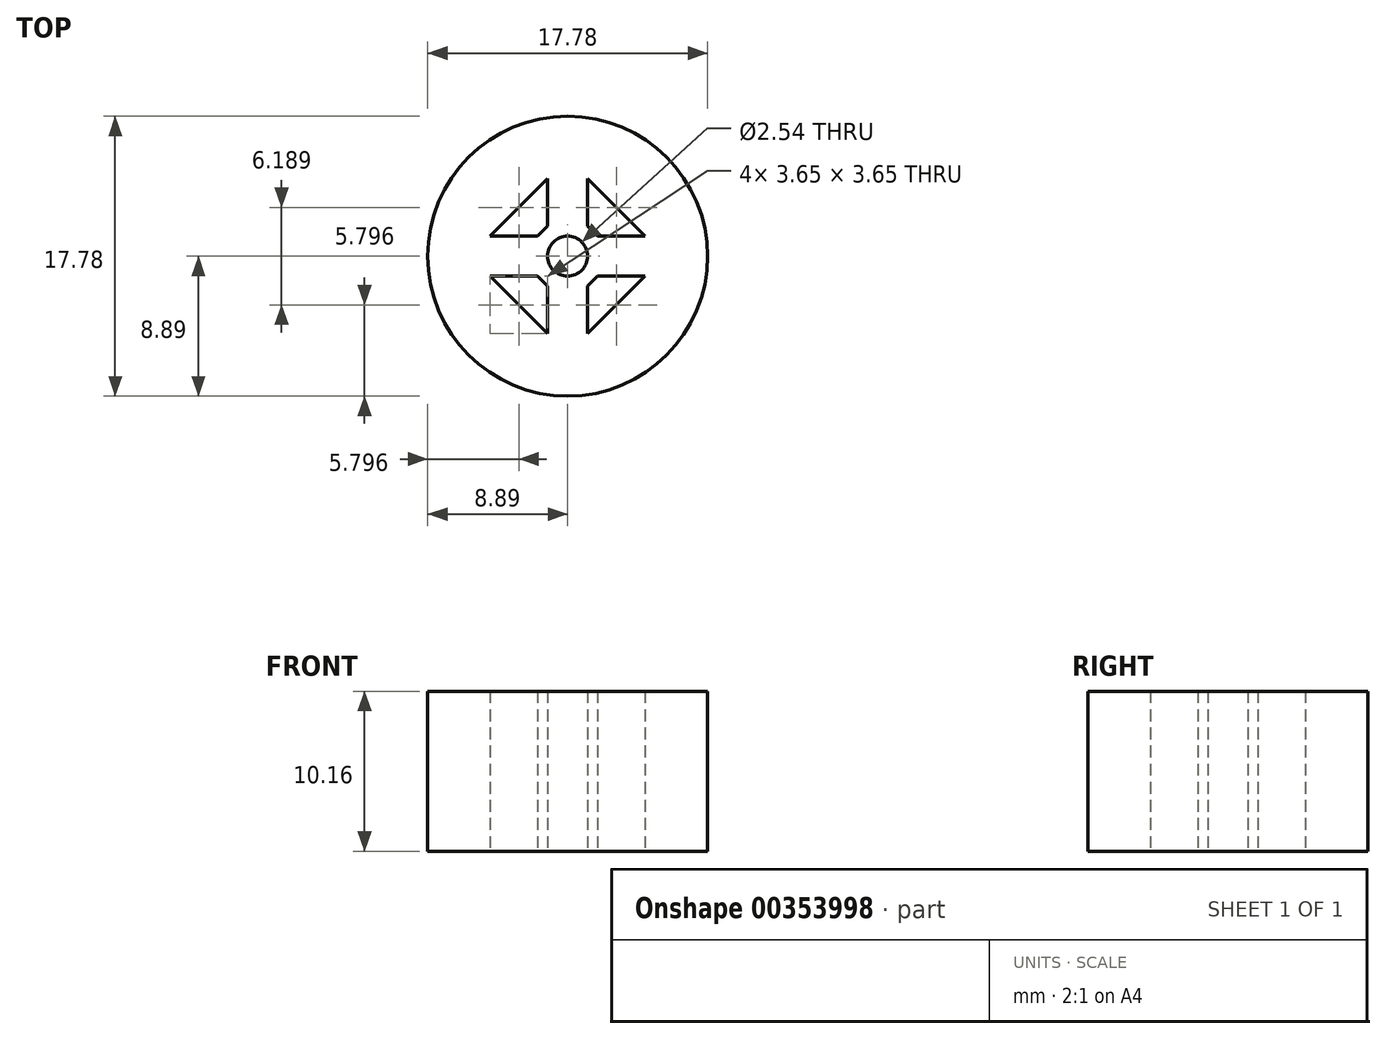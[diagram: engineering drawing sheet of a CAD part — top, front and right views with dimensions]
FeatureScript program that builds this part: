
annotation { "Feature Type Name" : "Feature", "Feature Type Description" : "" }
export const myFeature = defineFeature(function(context is Context, id is Id, definition is map)
    precondition{}
    {
        {
            var Q0;
            Q0=qCreatedBy(makeId("Top.planeOp"),FACE);
            var sketch = newSketch(context, id + "F0", { "sketchPlane" : qUnion([Q0])});
            skCircle(sketch, "E0", {"center": v(0, 0) * mm, "radius": 8.9 * mm});
            skCircle(sketch, "E1", {"center": v(0, 0) * mm, "radius": 1.27 * mm});
            skLineSegment(sketch, "E2", {"start": v(1.27, 1.9) * mm, "end": v(1.9, 1.27) * mm});
            skLineSegment(sketch, "E3", {"start": v(1.9, 1.27) * mm, "end": v(4.92, 1.27) * mm});
            skLineSegment(sketch, "E4", {"start": v(1.27, 1.9) * mm, "end": v(1.27, 4.92) * mm});
            skLineSegment(sketch, "E5", {"start": v(1.27, 4.92) * mm, "end": v(4.92, 1.27) * mm});
            skLineSegment(sketch, "E6.MirrorCS", {"start": v(-1.27, 4.92) * mm, "end": v(-4.92, 1.27) * mm});
            skLineSegment(sketch, "E7.MirrorCS", {"start": v(-1.27, 1.9) * mm, "end": v(-1.27, 4.92) * mm});
            skLineSegment(sketch, "E8.MirrorCS", {"start": v(-1.27, 1.9) * mm, "end": v(-1.9, 1.27) * mm});
            skLineSegment(sketch, "E9.MirrorCS", {"start": v(-1.9, 1.27) * mm, "end": v(-4.92, 1.27) * mm});
            skLineSegment(sketch, "E10.MirrorCS", {"start": v(-1.9, -1.27) * mm, "end": v(-4.92, -1.27) * mm});
            skLineSegment(sketch, "E11.MirrorCS", {"start": v(-1.27, -1.9) * mm, "end": v(-1.9, -1.27) * mm});
            skLineSegment(sketch, "E12.MirrorCS", {"start": v(-1.27, -1.9) * mm, "end": v(-1.27, -4.92) * mm});
            skLineSegment(sketch, "E13.MirrorCS", {"start": v(-1.27, -4.92) * mm, "end": v(-4.92, -1.27) * mm});
            skLineSegment(sketch, "E14.MirrorCS", {"start": v(1.27, -1.9) * mm, "end": v(1.27, -4.92) * mm});
            skLineSegment(sketch, "E15.MirrorCS", {"start": v(1.27, -4.92) * mm, "end": v(4.92, -1.27) * mm});
            skLineSegment(sketch, "E16.MirrorCS", {"start": v(1.9, -1.27) * mm, "end": v(4.92, -1.27) * mm});
            skLineSegment(sketch, "E17.MirrorCS", {"start": v(1.27, -1.9) * mm, "end": v(1.9, -1.27) * mm});
            skPoint(sketch, "E18.orphan", {"position": v(1.27, 0) * mm});
            skPoint(sketch, "E19.orphan", {"position": v(-1.27, 0) * mm});
            skPoint(sketch, "E20.end.orphan", {"position": v(0, 2.09) * mm});
            skPoint(sketch, "E20.start.orphan", {"position": v(0, 8.9) * mm});
            skSolve(sketch);
        }
        {
            var Q0;
            Q0 = qSketchRegion(id + "F0", true);
            extrude(context, id + "F1", {"entities" : qUnion([Q0]), "depth" : 10.16 * mm});
        }
    });
